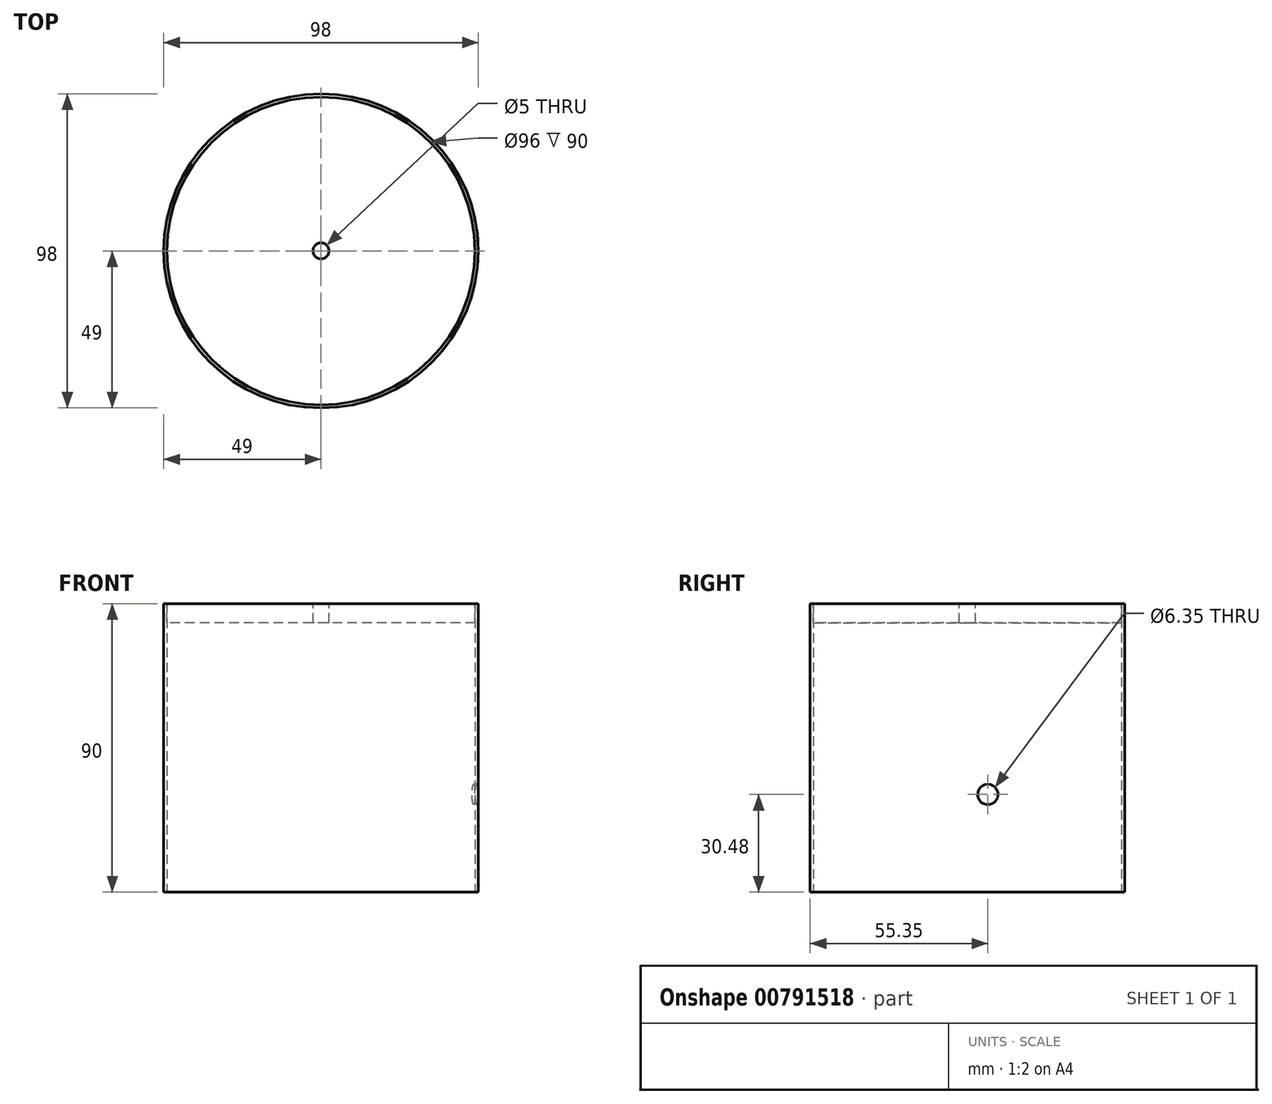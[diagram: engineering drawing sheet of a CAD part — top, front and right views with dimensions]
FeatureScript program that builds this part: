
annotation { "Feature Type Name" : "Feature", "Feature Type Description" : "" }
export const myFeature = defineFeature(function(context is Context, id is Id, definition is map)
    precondition{}
    {
        {
            var Q0;
            Q0=qCreatedBy(makeId("Top.planeOp"),FACE);
            var sketch = newSketch(context, id + "F0", { "sketchPlane" : qUnion([Q0])});
            skCircle(sketch, "E0", {"center": v(0, 0) * mm, "radius": 49 * mm});
            skCircle(sketch, "E1", {"center": v(0, 0) * mm, "radius": 48 * mm});
            skSolve(sketch);
        }
        {
            var Q0;
            Q0 = qSketchRegion(id + "F0", true);
            extrude(context, id + "F1", {"entities" : qUnion([Q0]), "depth" : 90 * mm, "offsetDistance" : 25.4 * mm});
        }
        {
            var Q0;
            Q0=makeQuery(id+"F1.opExtrude","CAP_FACE",FACE,{"disambiguationData":[OSD([sQuery(id+"F0.wireOp",EDGE,"E0"),sQuery(id+"F0.wireOp",EDGE,"E1")])],"isStart":false});
            var sketch = newSketch(context, id + "F2", { "sketchPlane" : qUnion([Q0])});
            skCircle(sketch, "E2", {"center": v(0, 0) * mm, "radius": 48 * mm});
            skCircle(sketch, "E3", {"center": v(0, 0) * mm, "radius": 2.5 * mm});
            skSolve(sketch);
        }
        {
            var Q0;
            Q0 = qSketchRegion(id + "F2", true);
            extrude(context, id + "F3", {"entities" : qUnion([Q0]), "oppositeDirection" : true, "depth" : 6 * mm, "offsetDistance" : 25.4 * mm});
        }
        {
            var Q0;
            Q0=qCreatedBy(makeId("Right.planeOp"),FACE);
            var sketch = newSketch(context, id + "F4", { "sketchPlane" : qUnion([Q0])});
            skCircle(sketch, "E4", {"center": v(6.35, 30.48) * mm, "radius": 3.18 * mm});
            skSolve(sketch);
        }
        {
            var Q0;
            Q0 = qSketchRegion(id + "F4", true);
            extrude(context, id + "F5", {"entities" : qUnion([Q0]), "operationType" : NewBodyOperationType.REMOVE, "depth" : 127 * mm, "offsetDistance" : 25.4 * mm});
        }
    });
